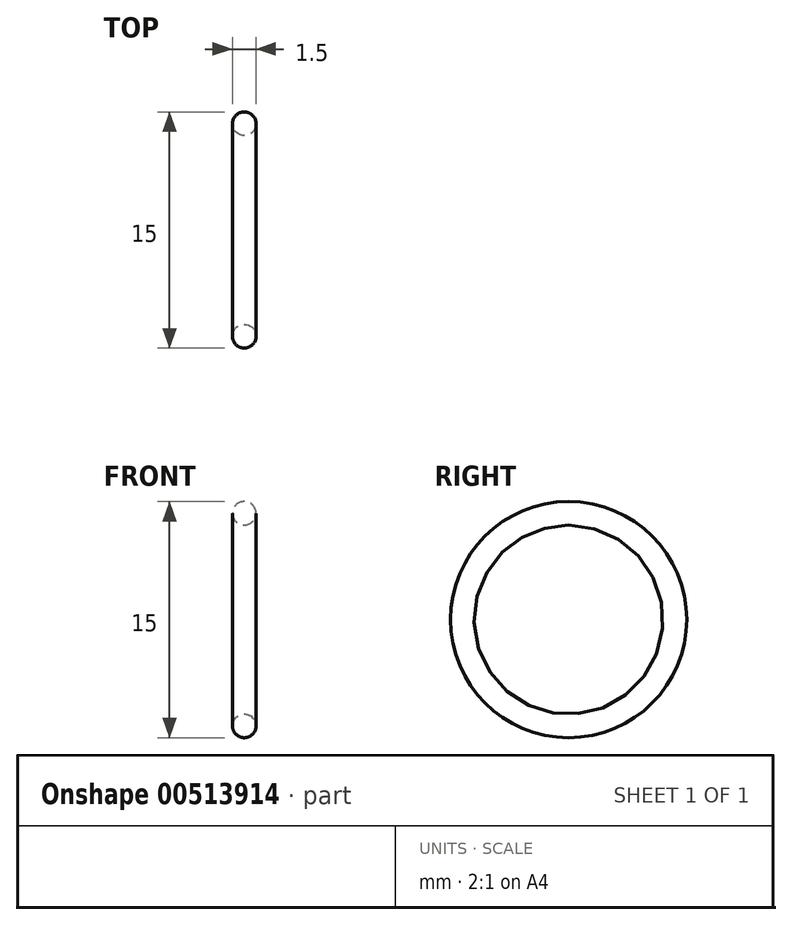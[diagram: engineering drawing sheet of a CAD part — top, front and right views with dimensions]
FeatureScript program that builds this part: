
annotation { "Feature Type Name" : "Feature", "Feature Type Description" : "" }
export const myFeature = defineFeature(function(context is Context, id is Id, definition is map)
    precondition{}
    {
        {
            var Q0;
            Q0=qCreatedBy(makeId("Right.planeOp"),FACE);
            var sketch = newSketch(context, id + "F0", { "sketchPlane" : qUnion([Q0])});
            skCircle(sketch, "E0", {"center": v(0, 0) * mm, "radius": 4 * mm});
            skSolve(sketch);
        }
        {
            var Q0;
            Q0=qCreatedBy(makeId("Top.planeOp"),FACE);
            var sketch = newSketch(context, id + "F1", { "sketchPlane" : qUnion([Q0])});
            skCircle(sketch, "E1", {"center": v(0, 6.75) * mm, "radius": 0.75 * mm});
            skSolve(sketch);
        }
        {
            var Q0;
            Q0=makeQuery(id+"F1.imprint","IMPRINT",FACE,{"disambiguationData":[TD([[makeQuery(id+"F1.imprint","IMPRINT",EDGE,{"derivedFrom":sQuery(id+"F1.wireOp",EDGE,"E1")}),1.0]])]});
            var Q1;
            Q1=sQuery(id+"F0.wireOp",EDGE,"E0");
            revolve(context, id + "F2", {"entities" : qUnion([Q0]), "axis" : qUnion([Q1]), "revolveType" : RevolveType.FULL});
        }
    });
